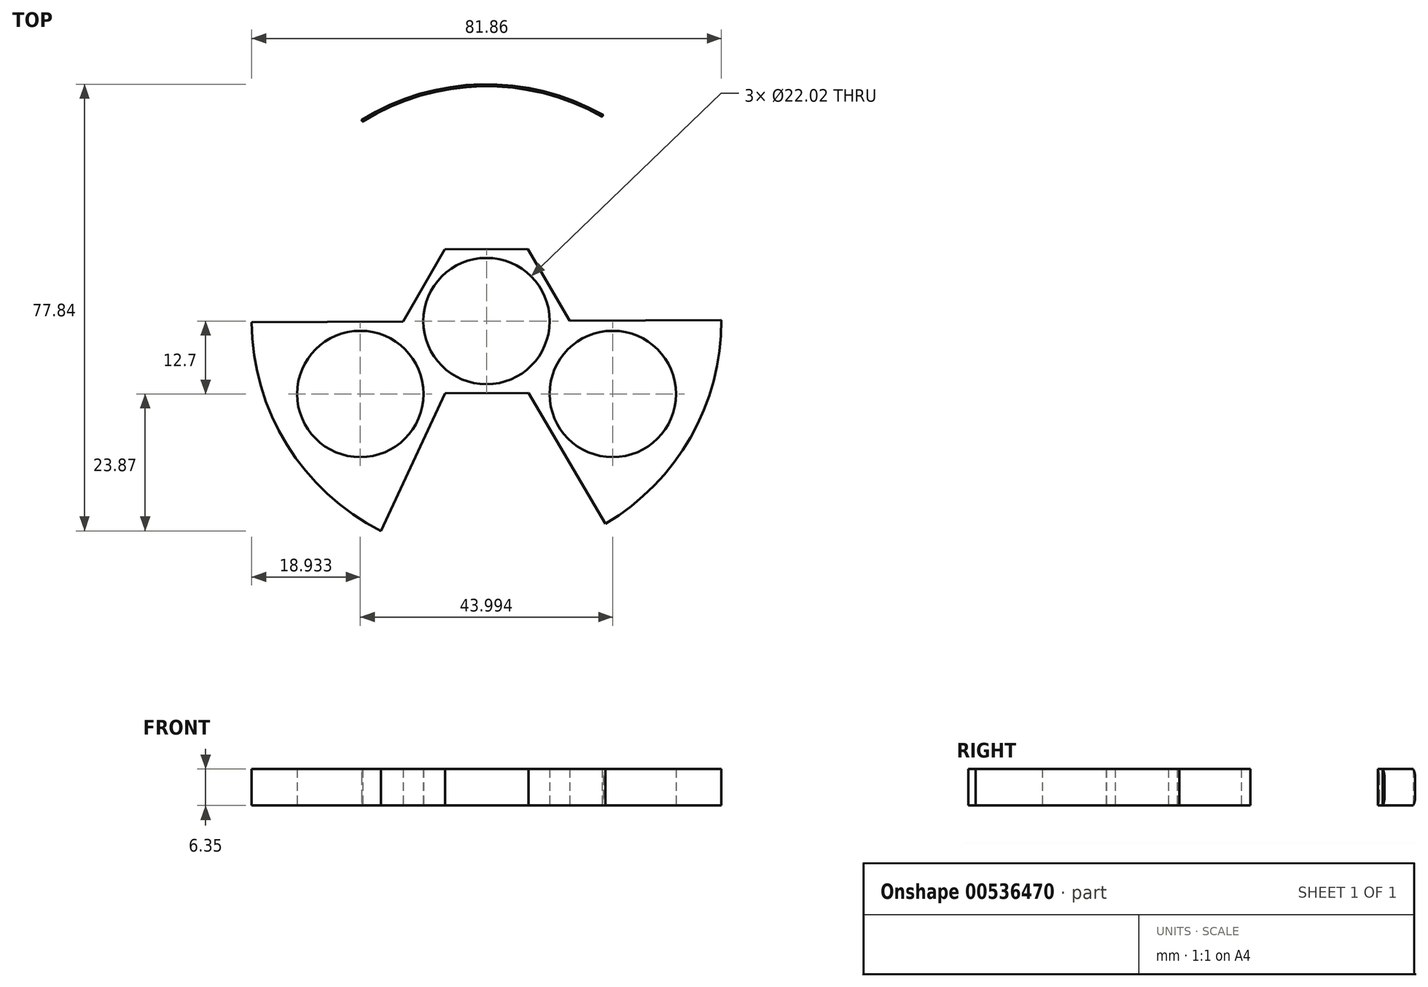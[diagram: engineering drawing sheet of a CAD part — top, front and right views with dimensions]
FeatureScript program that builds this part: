
annotation { "Feature Type Name" : "Feature", "Feature Type Description" : "" }
export const myFeature = defineFeature(function(context is Context, id is Id, definition is map)
    precondition{}
    {
        {
            var Q0;
            Q0=qCreatedBy(makeId("Top.planeOp"),FACE);
            var sketch = newSketch(context, id + "F0", { "sketchPlane" : qUnion([Q0])});
            skCircle(sketch, "E0", {"center": v(0, 0) * mm, "radius": 11.01 * mm});
            skArc(sketch, "E1", {"start": v(20.3, 35.93) * mm, "mid": v(-0.86, 41.26) * mm, "end": v(-21.79, 35.05) * mm});
            skCircle(sketch, "E2", {"center": v(0, 25.4) * mm, "radius": 11.01 * mm});
            skCircle(sketch, "E3.1.0", {"center": v(-22, -12.7) * mm, "radius": 11.01 * mm});
            skCircle(sketch, "E3.2.0", {"center": v(22, -12.7) * mm, "radius": 11.01 * mm});
            skCircle(sketch, "E4.cCircle", {"center": v(0, 0) * mm, "radius": 12.56 * mm, "construction": true});
            skLineSegment(sketch, "E4.0", {"start": v(14.5, 0.06) * mm, "end": v(7.3, -12.52) * mm});
            skLineSegment(sketch, "E4.1", {"start": v(7.3, -12.52) * mm, "end": v(-7.2, -12.59) * mm});
            skLineSegment(sketch, "E4.2", {"start": v(-7.2, -12.59) * mm, "end": v(-14.5, -0.06) * mm});
            skLineSegment(sketch, "E4.3", {"start": v(-14.5, -0.06) * mm, "end": v(-7.3, 12.52) * mm});
            skLineSegment(sketch, "E4.4", {"start": v(-7.3, 12.52) * mm, "end": v(7.2, 12.59) * mm});
            skLineSegment(sketch, "E4.5", {"start": v(7.2, 12.59) * mm, "end": v(14.5, 0.06) * mm});
            skPoint(sketch, "E4.0.midPoint", {"position": v(10.9, -6.23) * mm});
            skLineSegment(sketch, "E5", {"start": v(7.2, 12.59) * mm, "end": v(20.3, 35.93) * mm});
            skLineSegment(sketch, "E6", {"start": v(14.5, 0.06) * mm, "end": v(41.27, 0.18) * mm});
            skLineSegment(sketch, "E7", {"start": v(7.3, -12.52) * mm, "end": v(20.92, -35.57) * mm});
            skLineSegment(sketch, "E8", {"start": v(-7.2, -12.59) * mm, "end": v(-18.54, -36.87) * mm});
            skLineSegment(sketch, "E9", {"start": v(-14.5, -0.06) * mm, "end": v(-41.27, -0.18) * mm});
            skLineSegment(sketch, "E10", {"start": v(-7.3, 12.52) * mm, "end": v(-21.79, 35.05) * mm});
            skArc(sketch, "E11.trimOffspring", {"start": v(-41.27, -0.18) * mm, "mid": v(-35.08, -21.74) * mm, "end": v(-18.54, -36.87) * mm});
            skArc(sketch, "E12.trimOffspring", {"start": v(20.92, -35.57) * mm, "mid": v(35.87, -20.41) * mm, "end": v(41.27, 0.18) * mm});
            skCircle(sketch, "E13", {"center": v(0, 0) * mm, "radius": 40.93 * mm});
            skSolve(sketch);
        }
        {
            var Q0;
            Q0=makeQuery(id+"F0.imprint","IMPRINT",FACE,{"disambiguationData":[TD([[makeQuery(id+"F0.imprint","IMPRINT",EDGE,{"derivedFrom":sQuery(id+"F0.wireOp",EDGE,"E0")}),-1.0]])]});
            var Q1;
            Q1=makeQuery(id+"F0.imprint","IMPRINT",FACE,{"disambiguationData":[TD([[makeQuery(id+"F0.imprint","IMPRINT",EDGE,{"derivedFrom":sQuery(id+"F0.wireOp",EDGE,"E3.1.0")}),-1.0]])]});
            var Q2;
            Q2=makeQuery(id+"F0.imprint","IMPRINT",FACE,{"disambiguationData":[TD([[makeQuery(id+"F0.imprint","IMPRINT",EDGE,{"derivedFrom":sQuery(id+"F0.wireOp",EDGE,"E3.2.0")}),-1.0]])]});
            var Q3;
            Q3=makeQuery(id+"F0.imprint","IMPRINT",FACE,{"disambiguationData":[TD([[makeQuery(id+"F0.imprint","IMPRINT",EDGE,{"derivedFrom":sQuery(id+"F0.wireOp",EDGE,"E1")}),1.0]])]});
            extrude(context, id + "F1", {"entities" : qUnion([Q0, Q1, Q2, Q3]), "depth" : 6.35 * mm, "offsetDistance" : 25.4 * mm});
        }
        {
            var Q0;
            Q0=makeQuery(id+"F1.opExtrude","CAP_EDGE",EDGE,{"disambiguationData":[OSD([sQuery(id+"F0.wireOp",EDGE,"E12.trimOffspring")])],"isStart":false});
            var Q1;
            Q1=makeQuery(id+"F1.opExtrude","CAP_EDGE",EDGE,{"disambiguationData":[OSD([sQuery(id+"F0.wireOp",EDGE,"E12.trimOffspring")])],"isStart":true});
            var Q2;
            Q2=makeQuery(id+"F1.opExtrude","CAP_EDGE",EDGE,{"disambiguationData":[OSD([sQuery(id+"F0.wireOp",EDGE,"E11.trimOffspring")])],"isStart":false});
            var Q3;
            Q3=makeQuery(id+"F1.opExtrude","CAP_EDGE",EDGE,{"disambiguationData":[OSD([sQuery(id+"F0.wireOp",EDGE,"E11.trimOffspring")])],"isStart":true});
            var Q4;
            Q4=makeQuery(id+"F1.opExtrude","CAP_EDGE",EDGE,{"disambiguationData":[OSD([sQuery(id+"F0.wireOp",EDGE,"E1")])],"isStart":true});
            var Q5;
            Q5=makeQuery(id+"F1.opExtrude","CAP_EDGE",EDGE,{"disambiguationData":[OSD([sQuery(id+"F0.wireOp",EDGE,"E1")])],"isStart":false});
            fillet(context, id + "F2", {"entities" : qUnion([Q0, Q1, Q2, Q3, Q4, Q5]), "radius" : 2.54 * mm, "tangentPropagation" : true, "allowEdgeOverflow" : false});
        }
    });
